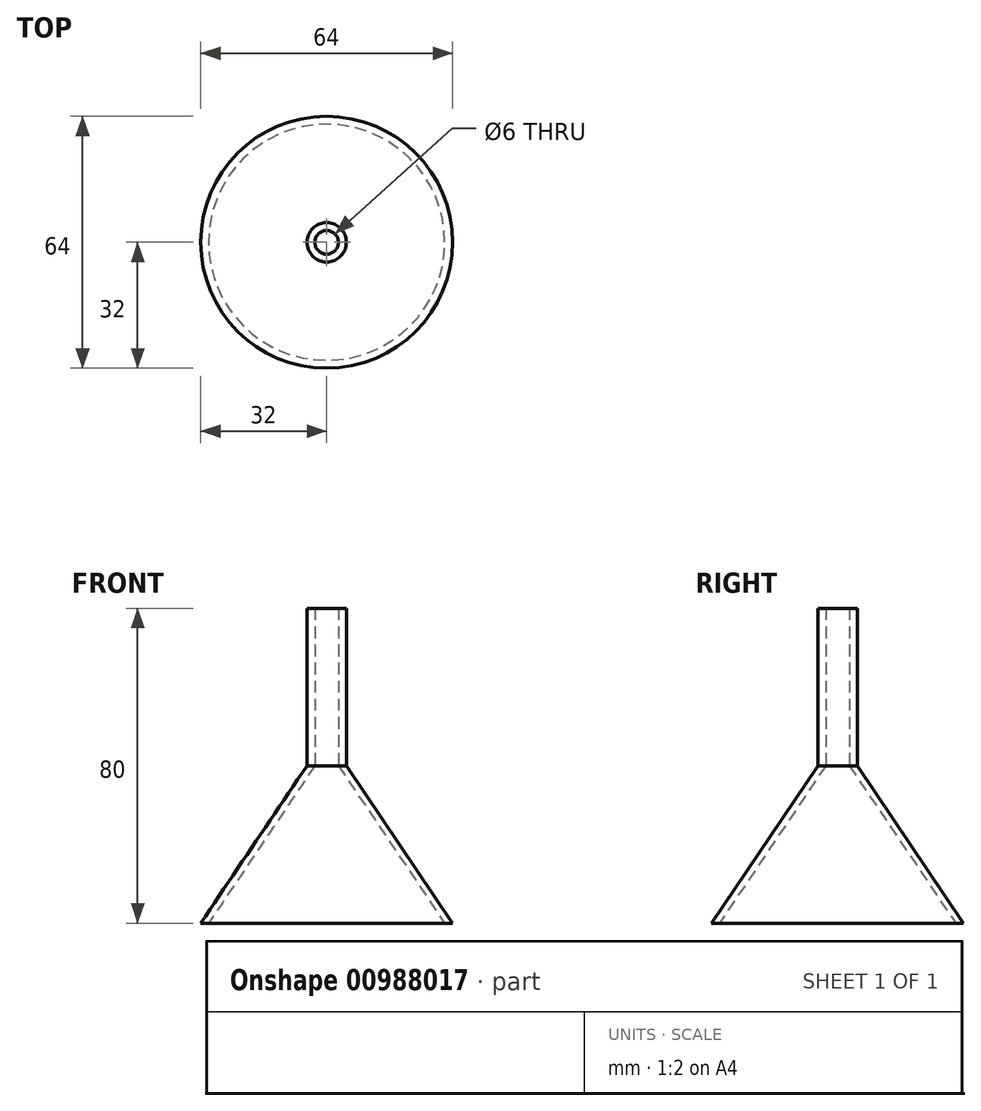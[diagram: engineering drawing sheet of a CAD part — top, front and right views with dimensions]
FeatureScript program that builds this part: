
annotation { "Feature Type Name" : "Feature", "Feature Type Description" : "" }
export const myFeature = defineFeature(function(context is Context, id is Id, definition is map)
    precondition{}
    {
        {
            var Q0;
            Q0=qCreatedBy(makeId("Front.planeOp"),FACE);
            var sketch = newSketch(context, id + "F0", { "sketchPlane" : qUnion([Q0])});
            skPoint(sketch, "E0", {"position": v(-32, 0) * mm});
            skPoint(sketch, "E1", {"position": v(-30, 0) * mm});
            skPoint(sketch, "E2", {"position": v(-5, 40) * mm});
            skPoint(sketch, "E3", {"position": v(-3, 40) * mm});
            skPoint(sketch, "E4", {"position": v(-3, 80) * mm});
            skPoint(sketch, "E5", {"position": v(-5, 80) * mm});
            skLineSegment(sketch, "E6", {"start": v(0, 0) * mm, "end": v(0, 88.48) * mm, "construction": true});
            skLineSegment(sketch, "E7", {"start": v(-5, 80) * mm, "end": v(-3, 80) * mm});
            skLineSegment(sketch, "E8", {"start": v(-3, 80) * mm, "end": v(-3, 40) * mm});
            skLineSegment(sketch, "E9", {"start": v(-3, 40) * mm, "end": v(-30, 0) * mm});
            skLineSegment(sketch, "E10", {"start": v(-30, 0) * mm, "end": v(-32, 0) * mm});
            skLineSegment(sketch, "E11", {"start": v(-5, 40) * mm, "end": v(-32, 0) * mm});
            skLineSegment(sketch, "E12", {"start": v(-5, 40) * mm, "end": v(-5, 80) * mm});
            skSolve(sketch);
        }
        {
            var Q0;
            Q0=makeQuery(id+"F0.imprint","IMPRINT",FACE,{"disambiguationData":[TD([[makeQuery(id+"F0.imprint","IMPRINT",EDGE,{"derivedFrom":sQuery(id+"F0.wireOp",EDGE,"E7")}),-1.0]])]});
            var Q1;
            Q1=sQuery(id+"F0.wireOp",EDGE,"E6");
            revolve(context, id + "F1", {"surfaceOperationType" : NewSurfaceOperationType.NEW, "entities" : qUnion([Q0]), "axis" : qUnion([Q1]), "revolveType" : RevolveType.FULL});
        }
    });
